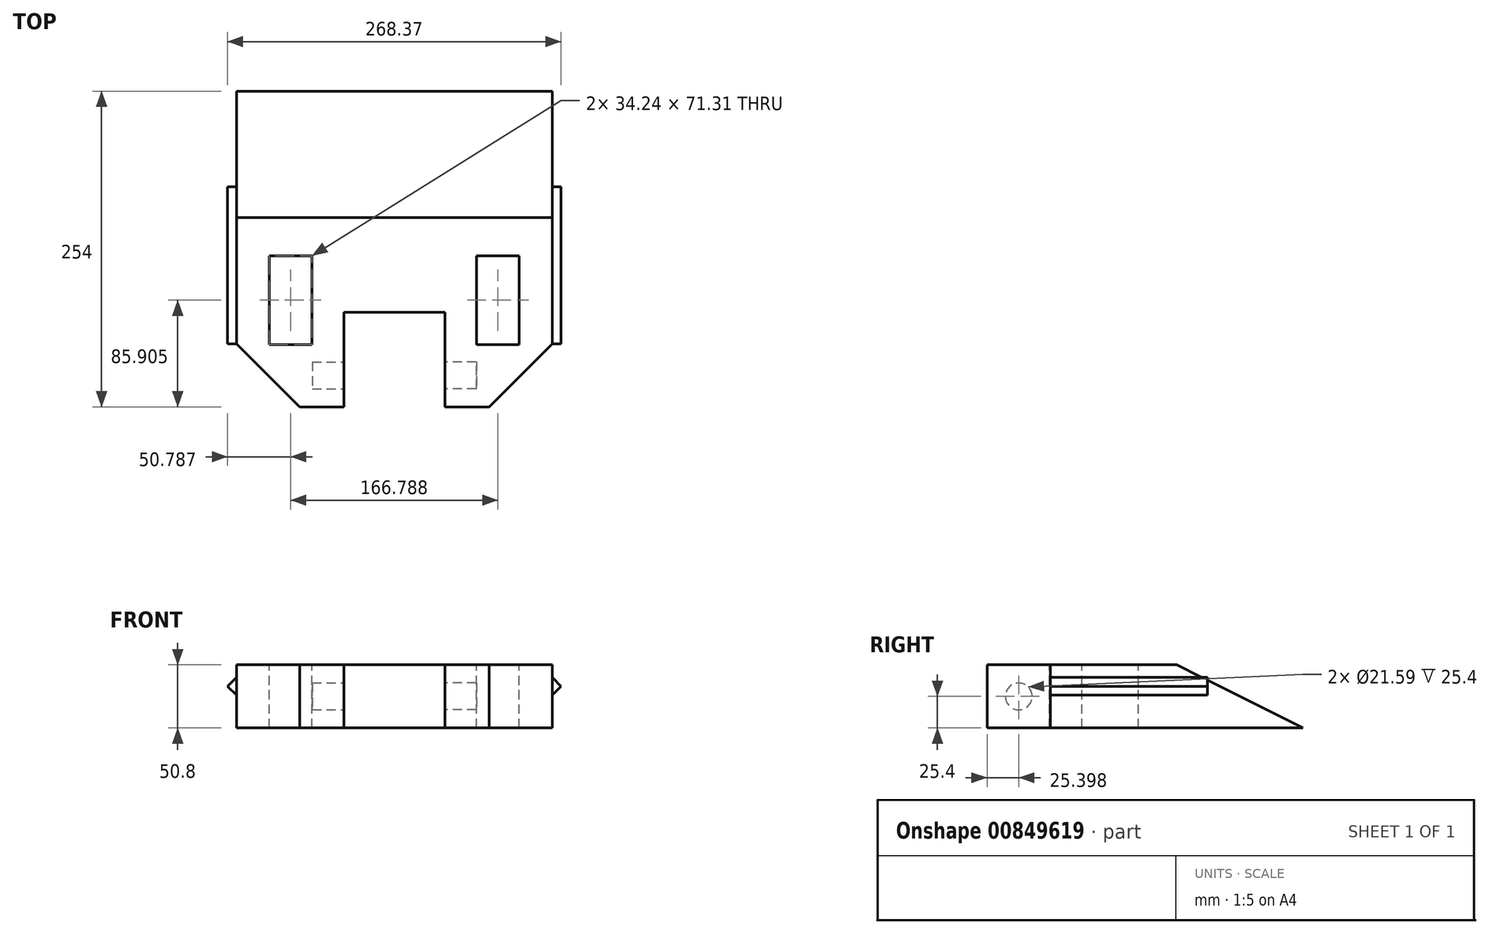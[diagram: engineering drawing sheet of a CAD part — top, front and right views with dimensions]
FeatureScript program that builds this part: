
annotation { "Feature Type Name" : "Feature", "Feature Type Description" : "" }
export const myFeature = defineFeature(function(context is Context, id is Id, definition is map)
    precondition{}
    {
        {
            var Q0;
            Q0=qCreatedBy(makeId("Top.planeOp"),FACE);
            var sketch = newSketch(context, id + "F0", { "sketchPlane" : qUnion([Q0])});
            skLineSegment(sketch, "E0.bottom", {"start": v(-45.7, 184.23) * mm, "end": v(208.3, 184.23) * mm});
            skLineSegment(sketch, "E0.top", {"start": v(5.1, -69.77) * mm, "end": v(157.5, -69.77) * mm});
            skLineSegment(sketch, "E0.left", {"start": v(-45.7, 184.23) * mm, "end": v(-45.7, -18.97) * mm});
            skLineSegment(sketch, "E0.right", {"start": v(208.3, 184.23) * mm, "end": v(208.3, -18.97) * mm});
            skLineSegment(sketch, "E1", {"start": v(-45.7, -18.97) * mm, "end": v(5.1, -69.77) * mm});
            skLineSegment(sketch, "E2", {"start": v(157.5, -69.77) * mm, "end": v(208.3, -18.97) * mm});
            skPoint(sketch, "E3.orphan", {"position": v(-45.7, -69.77) * mm});
            skPoint(sketch, "E4.orphan", {"position": v(208.3, -69.77) * mm});
            skSolve(sketch);
        }
        {
            var Q0;
            Q0=makeQuery(id+"F0.imprint","IMPRINT",FACE,{"disambiguationData":[TD([[makeQuery(id+"F0.imprint","IMPRINT",EDGE,{"derivedFrom":sQuery(id+"F0.wireOp",EDGE,"E0.bottom")}),-1.0]])]});
            extrude(context, id + "F1", {"entities" : qUnion([Q0]), "depth" : 50.8 * mm, "offsetDistance" : 25.4 * mm});
        }
        {
            var Q0;
            Q0=makeQuery(id+"F1.opExtrude","SWEPT_FACE",FACE,{"disambiguationData":[OSD([sQuery(id+"F0.wireOp",EDGE,"E0.right")])]});
            var sketch = newSketch(context, id + "F2", { "sketchPlane" : qUnion([Q0])});
            skLineSegment(sketch, "E5", {"start": v(184.23, 0) * mm, "end": v(82.63, 50.8) * mm});
            skLineSegment(sketch, "E6", {"start": v(82.63, 50.8) * mm, "end": v(184.23, 50.8) * mm});
            skLineSegment(sketch, "E7", {"start": v(184.23, 50.8) * mm, "end": v(184.23, 0) * mm});
            skSolve(sketch);
        }
        {
            var Q0;
            Q0=makeQuery(id+"F2.imprint","IMPRINT",FACE,{"disambiguationData":[TD([[makeQuery(id+"F2.imprint","IMPRINT",EDGE,{"derivedFrom":sQuery(id+"F2.wireOp",EDGE,"E5")}),-1.0]])]});
            extrude(context, id + "F3", {"entities" : qUnion([Q0]), "operationType" : NewBodyOperationType.REMOVE, "endBound" : BoundingType.THROUGH_ALL, "oppositeDirection" : true, "depth" : 25.4 * mm, "offsetDistance" : 25.4 * mm});
        }
        {
            var Q0;
            Q0=makeQuery(id+"F1.opExtrude","CAP_FACE",FACE,{"disambiguationData":[OSD([sQuery(id+"F0.wireOp",EDGE,"E0.bottom"),sQuery(id+"F0.wireOp",EDGE,"E0.left"),sQuery(id+"F0.wireOp",EDGE,"E0.right"),sQuery(id+"F0.wireOp",EDGE,"E1"),sQuery(id+"F0.wireOp",EDGE,"E0.top"),sQuery(id+"F0.wireOp",EDGE,"E2")])],"isStart":false});
            var sketch = newSketch(context, id + "F4", { "sketchPlane" : qUnion([Q0])});
            skLineSegment(sketch, "E8.bottom", {"start": v(40.66, -69.77) * mm, "end": v(121.94, -69.77) * mm});
            skLineSegment(sketch, "E8.top", {"start": v(40.66, 6.43) * mm, "end": v(121.94, 6.43) * mm});
            skLineSegment(sketch, "E8.left", {"start": v(40.66, -69.77) * mm, "end": v(40.66, 6.43) * mm});
            skLineSegment(sketch, "E8.right", {"start": v(121.94, -69.77) * mm, "end": v(121.94, 6.43) * mm});
            skSolve(sketch);
        }
        {
            var Q0;
            Q0=makeQuery(id+"F4.imprint","IMPRINT",FACE,{"disambiguationData":[TD([[makeQuery(id+"F4.imprint","IMPRINT",EDGE,{"derivedFrom":sQuery(id+"F4.wireOp",EDGE,"E8.bottom")}),1.0]])]});
            extrude(context, id + "F5", {"entities" : qUnion([Q0]), "operationType" : NewBodyOperationType.REMOVE, "endBound" : BoundingType.THROUGH_ALL, "oppositeDirection" : true, "depth" : 25.4 * mm, "offsetDistance" : 25.4 * mm});
        }
        {
            var Q0;
            {var subQ0=sQuery(id+"F0.wireOp",EDGE,"E2");var subQ1=sQuery(id+"F0.wireOp",EDGE,"E0.top");Q0=makeQuery(id+"F5.boolean.opBoolean","SPLIT",FACE,{"disambiguationData":[TD([makeQuery(id+"F1.opExtrude","SWEPT_FACE",FACE,{"disambiguationData":[OSD([subQ0])]})])],"derivedFrom":makeQuery(id+"F1.opExtrude","SWEPT_FACE",FACE,{"disambiguationData":[OSD([subQ1])]})});}
            var sketch = newSketch(context, id + "F6", { "sketchPlane" : qUnion([Q0])});
            skLineSegment(sketch, "E9", {"start": v(-45.7, 26.4) * mm, "end": v(-52.88, 33.58) * mm});
            skLineSegment(sketch, "E10", {"start": v(-52.88, 33.58) * mm, "end": v(-45.7, 40.77) * mm});
            skLineSegment(sketch, "E11", {"start": v(81.3, 76.58) * mm, "end": v(81.3, 0) * mm});
            skLineSegment(sketch, "E12.MirrorCS", {"start": v(215.49, 33.58) * mm, "end": v(208.3, 40.77) * mm});
            skLineSegment(sketch, "E13.MirrorCS", {"start": v(208.3, 26.4) * mm, "end": v(215.49, 33.58) * mm});
            skLineSegment(sketch, "E14", {"start": v(-45.7, 40.77) * mm, "end": v(-45.7, 26.4) * mm});
            skLineSegment(sketch, "E15", {"start": v(208.3, 40.77) * mm, "end": v(208.3, 26.4) * mm});
            skSolve(sketch);
        }
        {
            var Q0;
            Q0=makeQuery(id+"F6.imprint","IMPRINT",FACE,{"disambiguationData":[TD([[makeQuery(id+"F6.imprint","IMPRINT",EDGE,{"derivedFrom":sQuery(id+"F6.wireOp",EDGE,"E9")}),-1.0]])]});
            var Q1;
            Q1=makeQuery(id+"F6.imprint","IMPRINT",FACE,{"disambiguationData":[TD([[makeQuery(id+"F6.imprint","IMPRINT",EDGE,{"derivedFrom":sQuery(id+"F6.wireOp",EDGE,"E15")}),1.0]])]});
            extrude(context, id + "F7", {"entities" : qUnion([Q0, Q1]), "operationType" : NewBodyOperationType.ADD, "oppositeDirection" : true, "depth" : 177.04 * mm, "offsetDistance" : 25.4 * mm});
        }
        {
            var Q0;
            Q0=makeQuery(id+"F1.opExtrude","CAP_FACE",FACE,{"disambiguationData":[OSD([sQuery(id+"F0.wireOp",EDGE,"E0.bottom"),sQuery(id+"F0.wireOp",EDGE,"E0.left"),sQuery(id+"F0.wireOp",EDGE,"E0.right"),sQuery(id+"F0.wireOp",EDGE,"E1"),sQuery(id+"F0.wireOp",EDGE,"E0.top"),sQuery(id+"F0.wireOp",EDGE,"E2")])],"isStart":false});
            var sketch = newSketch(context, id + "F8", { "sketchPlane" : qUnion([Q0])});
            skLineSegment(sketch, "E16.bottom", {"start": v(-45.7, -18.97) * mm, "end": v(-59.9, -18.97) * mm});
            skLineSegment(sketch, "E16.top", {"start": v(-45.7, -73.5) * mm, "end": v(-59.9, -73.5) * mm});
            skLineSegment(sketch, "E16.left", {"start": v(-45.7, -18.97) * mm, "end": v(-45.7, -73.5) * mm});
            skLineSegment(sketch, "E16.right", {"start": v(-59.9, -18.97) * mm, "end": v(-59.9, -73.5) * mm});
            skLineSegment(sketch, "E17.bottom", {"start": v(208.3, -18.97) * mm, "end": v(233.38, -18.97) * mm});
            skLineSegment(sketch, "E17.top", {"start": v(208.3, -75.11) * mm, "end": v(233.38, -75.11) * mm});
            skLineSegment(sketch, "E17.left", {"start": v(208.3, -18.97) * mm, "end": v(208.3, -75.11) * mm});
            skLineSegment(sketch, "E17.right", {"start": v(233.38, -18.97) * mm, "end": v(233.38, -75.11) * mm});
            skSolve(sketch);
        }
        {
            var Q0;
            Q0=makeQuery(id+"F8.imprint","IMPRINT",FACE,{"disambiguationData":[TD([[makeQuery(id+"F8.imprint","IMPRINT",EDGE,{"derivedFrom":sQuery(id+"F8.wireOp",EDGE,"E16.bottom")}),1.0]])]});
            var Q1;
            Q1=makeQuery(id+"F8.imprint","IMPRINT",FACE,{"disambiguationData":[TD([[makeQuery(id+"F8.imprint","IMPRINT",EDGE,{"derivedFrom":sQuery(id+"F8.wireOp",EDGE,"E17.bottom")}),-1.0]])]});
            extrude(context, id + "F9", {"entities" : qUnion([Q0, Q1]), "operationType" : NewBodyOperationType.REMOVE, "endBound" : BoundingType.THROUGH_ALL, "oppositeDirection" : true, "depth" : 25.4 * mm, "offsetDistance" : 25.4 * mm});
        }
        {
            var Q0;
            Q0=makeQuery(id+"F1.opExtrude","CAP_FACE",FACE,{"disambiguationData":[OSD([sQuery(id+"F0.wireOp",EDGE,"E0.bottom"),sQuery(id+"F0.wireOp",EDGE,"E0.left"),sQuery(id+"F0.wireOp",EDGE,"E0.right"),sQuery(id+"F0.wireOp",EDGE,"E1"),sQuery(id+"F0.wireOp",EDGE,"E0.top"),sQuery(id+"F0.wireOp",EDGE,"E2")])],"isStart":false});
            var sketch = newSketch(context, id + "F10", { "sketchPlane" : qUnion([Q0])});
            skPoint(sketch, "E18", {"position": v(81.3, 6.43) * mm});
            skLineSegment(sketch, "E19", {"start": v(81.3, 6.43) * mm, "end": v(81.3, -67.86) * mm});
            skLineSegment(sketch, "E20.bottom", {"start": v(-19.22, 51.79) * mm, "end": v(15.03, 51.79) * mm});
            skLineSegment(sketch, "E20.top", {"start": v(-19.22, -19.52) * mm, "end": v(15.03, -19.52) * mm});
            skLineSegment(sketch, "E20.left", {"start": v(-19.22, 51.79) * mm, "end": v(-19.22, -19.52) * mm});
            skLineSegment(sketch, "E20.right", {"start": v(15.03, 51.79) * mm, "end": v(15.03, -19.52) * mm});
            skLineSegment(sketch, "E21.MirrorCS", {"start": v(181.82, 51.79) * mm, "end": v(181.82, -19.52) * mm});
            skLineSegment(sketch, "E22.MirrorCS", {"start": v(147.57, 51.79) * mm, "end": v(147.57, -19.52) * mm});
            skLineSegment(sketch, "E23.MirrorCS", {"start": v(181.82, 51.79) * mm, "end": v(147.57, 51.79) * mm});
            skLineSegment(sketch, "E24.MirrorCS", {"start": v(181.82, -19.52) * mm, "end": v(147.57, -19.52) * mm});
            skSolve(sketch);
        }
        {
            var Q0;
            Q0=makeQuery(id+"F10.imprint","IMPRINT",FACE,{"disambiguationData":[TD([[makeQuery(id+"F10.imprint","IMPRINT",EDGE,{"derivedFrom":sQuery(id+"F10.wireOp",EDGE,"leNyJGLs-Vims-kSCW-DAYb-5UrLLI0laFL2.bottom")}),-1.0]])]});
            var Q1;
            Q1=makeQuery(id+"F10.imprint","IMPRINT",FACE,{"disambiguationData":[TD([[makeQuery(id+"F10.imprint","IMPRINT",EDGE,{"derivedFrom":sQuery(id+"F10.wireOp",EDGE,"ltuC3uon-IMQP-zXnW-Vewq-F6LHG07oQVlK.bottom")}),-1.0]])]});
            var Q2;
            Q2=makeQuery(id+"F10.imprint","IMPRINT",FACE,{"disambiguationData":[TD([[makeQuery(id+"F10.imprint","IMPRINT",EDGE,{"derivedFrom":sQuery(id+"F10.wireOp",EDGE,"e504860c-a273-4c84-ad37-268107979db30.MirrorCS")}),-1.0]])]});
            var Q3;
            Q3=makeQuery(id+"F10.imprint","IMPRINT",FACE,{"disambiguationData":[TD([[makeQuery(id+"F10.imprint","IMPRINT",EDGE,{"derivedFrom":sQuery(id+"F10.wireOp",EDGE,"E20.bottom")}),-1.0]])]});
            var Q4;
            Q4=makeQuery(id+"F10.imprint","IMPRINT",FACE,{"disambiguationData":[TD([[makeQuery(id+"F10.imprint","IMPRINT",EDGE,{"derivedFrom":sQuery(id+"F10.wireOp",EDGE,"E21.MirrorCS")}),-1.0]])]});
            extrude(context, id + "F11", {"entities" : qUnion([Q0, Q1, Q2, Q3, Q4]), "operationType" : NewBodyOperationType.REMOVE, "endBound" : BoundingType.THROUGH_ALL, "oppositeDirection" : true, "depth" : 25.4 * mm, "offsetDistance" : 25.4 * mm});
        }
        {
            var Q0;
            Q0=makeQuery(id+"F5.boolean.opBoolean","COPY",FACE,{"derivedFrom":makeQuery(id+"F5.opExtrude","SWEPT_FACE",FACE,{"disambiguationData":[OSD([sQuery(id+"F4.wireOp",EDGE,"E8.left")])]})});
            var sketch = newSketch(context, id + "F12", { "sketchPlane" : qUnion([Q0])});
            skCircle(sketch, "E25", {"center": v(-44.37, 25.4) * mm, "radius": 10.8 * mm});
            skSolve(sketch);
        }
        {
            var Q0;
            Q0=makeQuery(id+"F12.imprint","IMPRINT",FACE,{"disambiguationData":[TD([[makeQuery(id+"F12.imprint","IMPRINT",EDGE,{"derivedFrom":sQuery(id+"F12.wireOp",EDGE,"E25")}),1.0]])]});
            extrude(context, id + "F13", {"entities" : qUnion([Q0]), "operationType" : NewBodyOperationType.REMOVE, "oppositeDirection" : true, "depth" : 25.4 * mm, "offsetDistance" : 25.4 * mm});
        }
        {
            var Q0;
            Q0=makeQuery(id+"F5.boolean.opBoolean","COPY",FACE,{"derivedFrom":makeQuery(id+"F5.opExtrude","SWEPT_FACE",FACE,{"disambiguationData":[OSD([sQuery(id+"F4.wireOp",EDGE,"E8.right")])]})});
            var sketch = newSketch(context, id + "F14", { "sketchPlane" : qUnion([Q0])});
            skCircle(sketch, "E26", {"center": v(44.37, 25.4) * mm, "radius": 10.8 * mm});
            skSolve(sketch);
        }
        {
            var Q0;
            Q0=makeQuery(id+"F14.imprint","IMPRINT",FACE,{"disambiguationData":[TD([[makeQuery(id+"F14.imprint","IMPRINT",EDGE,{"derivedFrom":sQuery(id+"F14.wireOp",EDGE,"E26")}),1.0]])]});
            extrude(context, id + "F15", {"entities" : qUnion([Q0]), "operationType" : NewBodyOperationType.REMOVE, "oppositeDirection" : true, "depth" : 25.4 * mm, "offsetDistance" : 25.4 * mm});
        }
    });
